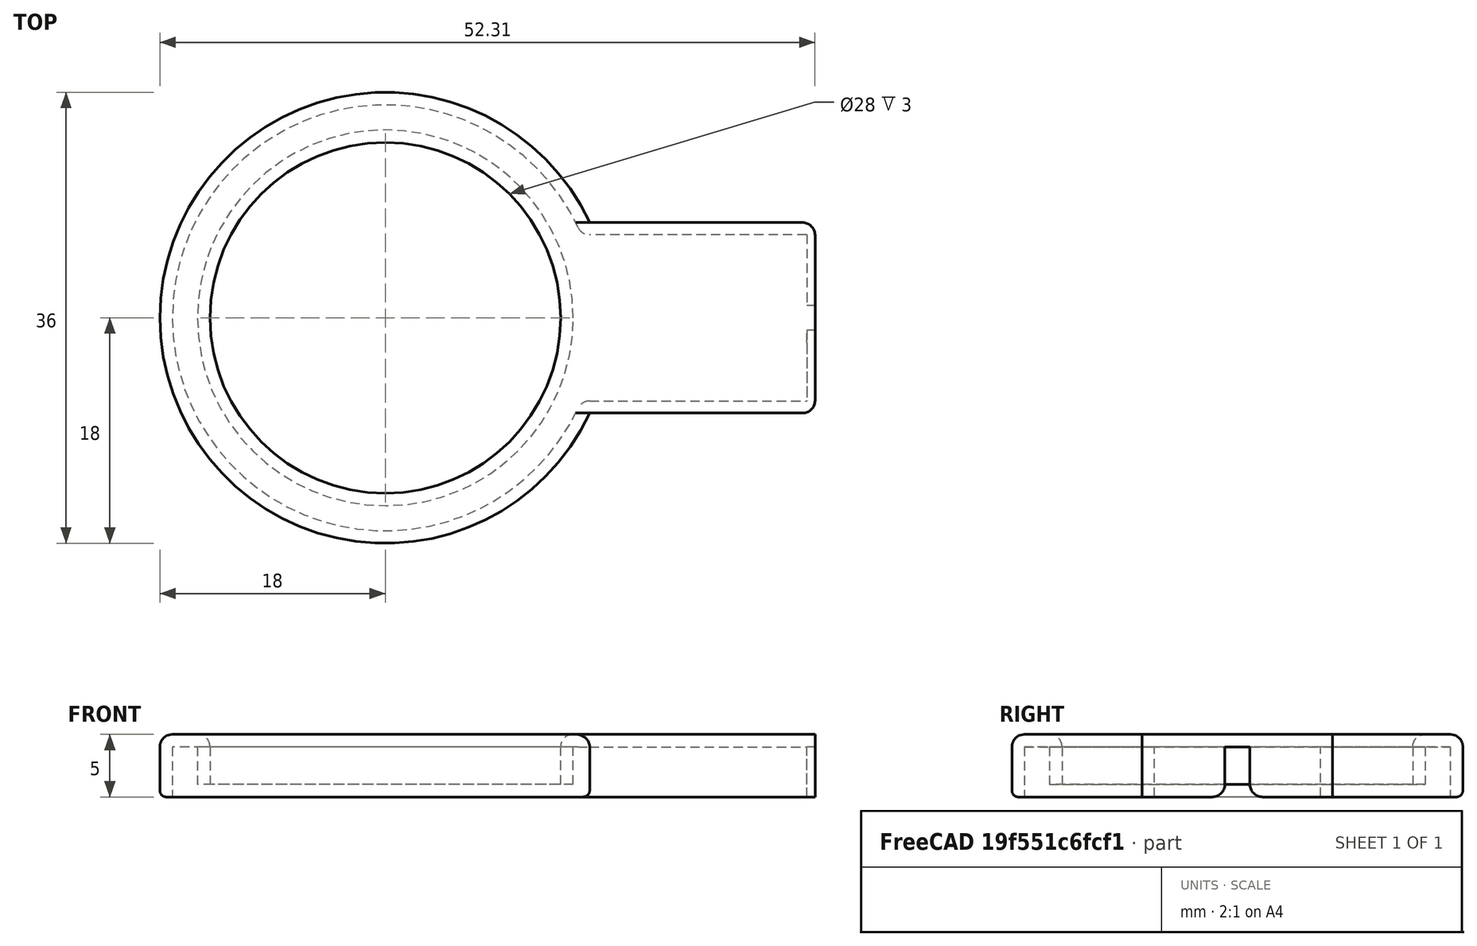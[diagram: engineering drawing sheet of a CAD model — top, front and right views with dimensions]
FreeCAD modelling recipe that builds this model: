
FCSTD DOCUMENT  (FreeCAD 0.19R24291 (Git))
Label: bruker7t_fus_single_coil2_case
License: All rights reserved
LicenseURL: http://en.wikipedia.org/wiki/All_rights_reserved
objects: PartDesign::Fillet×9, TechDraw::DrawViewDimension×7, Sketcher::SketchObject×4, PartDesign::Pad×2, PartDesign::Pocket×2, App::Part×1, PartDesign::Body×1, TechDraw::DrawSVGTemplate×1, TechDraw::DrawViewPart×1, TechDraw::DrawPage×1
note: 31 computed .brp shape members not serialized (recipe doc carries the construction recipe); baked Part::Feature solids carry a one-line shape summary decoded from their .brp

FEATURE [Sketcher::SketchObject] Sketch001
  FullyConstrained = true
  MapMode = 5
  sketch-geometry (5):
    g0: LineSegment StartX=29.3135 StartY=7.60713 StartZ=0 EndX=11.3135 EndY=7.60713 EndZ=0
    g1: ArcOfCircle CenterX=-5 CenterY=-1.8e-15 CenterZ=0 NormalX=0 NormalY=0 NormalZ=1 AngleXU=0 Radius=18 StartAngle=0.436332 EndAngle=5.84685
    g2: LineSegment StartX=11.3135 StartY=-7.60713 StartZ=0 EndX=29.3135 EndY=-7.60713 EndZ=0
    g3: LineSegment StartX=-5 StartY=-1.8e-15 StartZ=0 EndX=11.3135 EndY=7.60713 EndZ=0
    g4: LineSegment StartX=29.3135 StartY=7.60713 StartZ=0 EndX=29.3135 EndY=-7.60713 EndZ=0
  constraints (15):
    c: Horizontal(g0)
    c: Coincident(g1,g2)
    c: Horizontal(g2)
    c: Equal(g0,g2)
    c: PointOnObject(g1,g-1)
    c: Radius(g1) = 18
    c: Coincident(g0,g1)
    c: Coincident(g3,g1)
    c: Coincident(g3,g0)
    c: Angle(g-1,g3) = 0.436332
    c: DistanceX(g1,g-1) = 5
    c: DistanceX(g2,g2) = 18
    c: Coincident(g4,g0)
    c: Coincident(g4,g2)
    c: Symmetric(g0,g2,g-1)
FEATURE [Sketcher::SketchObject] Sketch004
  FullyConstrained = true
  MapMode = 5
  sketch-geometry (10):
    g0: Circle CenterX=-5 CenterY=-2.84e-14 CenterZ=0 NormalX=0 NormalY=0 NormalZ=1 AngleXU=0 Radius=16
    g1: LineSegment StartX=28.6486 StartY=6.64243 StartZ=0 EndX=10.6486 EndY=6.64243 EndZ=0
    g2: ArcOfCircle CenterX=-5 CenterY=-2.84e-14 CenterZ=0 NormalX=0 NormalY=0 NormalZ=1 AngleXU=0 Radius=17 StartAngle=0.401426 EndAngle=5.88176
    g3: LineSegment StartX=10.6486 StartY=-6.64243 StartZ=0 EndX=28.6486 EndY=-6.64243 EndZ=0
    g4: LineSegment StartX=10.6486 StartY=-6.64243 StartZ=0 EndX=-5 EndY=-2.84e-14 EndZ=0
    g5: LineSegment StartX=28.6486 StartY=6.64243 StartZ=0 EndX=28.6486 EndY=1 EndZ=0
    g6: LineSegment StartX=28.6486 StartY=1 StartZ=0 EndX=32.6486 EndY=1 EndZ=0
    g7: LineSegment StartX=32.6486 StartY=1 StartZ=0 EndX=32.6486 EndY=-1 EndZ=0
    g8: LineSegment StartX=32.6486 StartY=-1 StartZ=0 EndX=28.6486 EndY=-1 EndZ=0
    g9: LineSegment StartX=28.6486 StartY=-1 StartZ=0 EndX=28.6486 EndY=-6.64243 EndZ=0
  constraints (27):
    c: Radius(g0) = 16
    c: DistanceX(g0,g-1) = 5
    c: Horizontal(g1)
    c: Coincident(g2,g3)
    c: Horizontal(g3)
    c: Coincident(g2,g1)
    c: Coincident(g2,g0)
    c: Radius(g2) = 17
    c: Symmetric(g2,g1,g-1)
    c: DistanceX(g1,g1) = 18
    c: Coincident(g4,g2)
    c: Coincident(g4,g2)
    c: Angle(g4,g-1) = 0.401426
    c: Equal(g3,g1)
    c: Coincident(g1,g5)
    c: Vertical(g5)
    c: Coincident(g5,g6)
    c: Horizontal(g6)
    c: Coincident(g6,g7)
    c: Coincident(g7,g8)
    c: Horizontal(g8)
    c: Coincident(g8,g9)
    c: Coincident(g9,g3)
    c: Vertical(g9)
    c: Symmetric(g6,g7,g-1)
    c: DistanceY(g7,g7) = 2
    c: DistanceX(g6,g6) = 4
FEATURE [App::Part] Part
  Origin = -> Origin
FEATURE [PartDesign::Pad] Pad
  Direction = (1,1,1)
  Length = 5
  Length2 = 100
  Profile = -> Sketch001
  Refine = true
  Type = 0
FEATURE [PartDesign::Pocket] Pocket
  BaseFeature = -> Pad
  Length = 4
  Length2 = 100
  Profile = -> Sketch004
  Refine = true
  Reversed = true
  Type = 0
FEATURE [Sketcher::SketchObject] Sketch005
  FullyConstrained = true
  MapMode = 5
  Placement = pos=(0,0,1) rot=(0,0,1;0rad)
  sketch-geometry (2):
    g0: Circle CenterX=-5 CenterY=0 CenterZ=0 NormalX=0 NormalY=0 NormalZ=1 AngleXU=0 Radius=16
    g1: Circle CenterX=-5 CenterY=0 CenterZ=0 NormalX=0 NormalY=0 NormalZ=1 AngleXU=0 Radius=15
  constraints (5):
    c: Radius(g0) = 16
    c: PointOnObject(g0,g-1)
    c: DistanceX(g0,g-1) = 5
    c: Coincident(g0,g1)
    c: Radius(g1) = 15
FEATURE [Sketcher::SketchObject] Sketch006
  FullyConstrained = true
  MapMode = 5
  sketch-geometry (2):
    g0: Circle CenterX=-5 CenterY=0 CenterZ=0 NormalX=0 NormalY=0 NormalZ=1 AngleXU=0 Radius=16
    g1: Circle CenterX=-5 CenterY=0 CenterZ=0 NormalX=0 NormalY=0 NormalZ=1 AngleXU=0 Radius=14
  constraints (5):
    c: Radius(g0) = 16
    c: PointOnObject(g0,g-1)
    c: DistanceX(g0,g-1) = 5
    c: Coincident(g0,g1)
    c: Radius(g1) = 14
FEATURE [PartDesign::Pad] Pad001
  BaseFeature = -> Pocket
  Direction = (1,1,1)
  Length = 4
  Length2 = 100
  Profile = -> Sketch005
  Refine = true
  Type = 0
FEATURE [PartDesign::Fillet] Fillet
  Base = -> Pad001 [Edge14]
  BaseFeature = -> Pad001
  Radius = 1
  Refine = true
  SupportTransform = false
FEATURE [PartDesign::Fillet] Fillet001
  Base = -> Fillet [Edge8]
  BaseFeature = -> Fillet
  Radius = 0.5
  Refine = true
  SupportTransform = false
FEATURE [PartDesign::Pocket] Pocket001
  BaseFeature = -> Fillet001
  Length = 5
  Length2 = 100
  Profile = -> Sketch006
  Refine = true
  Reversed = true
  Type = 1
FEATURE [PartDesign::Fillet] Fillet002
  Base = -> Pocket001 [Edge30]
  BaseFeature = -> Pocket001
  Radius = 1
  Refine = true
  SupportTransform = false
FEATURE [PartDesign::Fillet] Fillet003
  Base = -> Fillet002 [Edge32]
  BaseFeature = -> Fillet002
  Radius = 1
  Refine = true
  SupportTransform = false
FEATURE [PartDesign::Fillet] Fillet004
  Base = -> Fillet003 [Edge21]
  BaseFeature = -> Fillet003
  Radius = 1
  Refine = true
  SupportTransform = false
FEATURE [PartDesign::Fillet] Fillet005
  Base = -> Fillet004 [Edge10]
  BaseFeature = -> Fillet004
  Radius = 1
  Refine = true
  SupportTransform = false
FEATURE [PartDesign::Fillet] Fillet006
  Base = -> Fillet005 [Edge3]
  BaseFeature = -> Fillet005
  Radius = 1
  Refine = true
  SupportTransform = false
FEATURE [PartDesign::Fillet] Fillet007
  Base = -> Fillet006 [Edge61]
  BaseFeature = -> Fillet006
  Radius = 1
  Refine = true
  SupportTransform = false
FEATURE [PartDesign::Fillet] Fillet008
  Base = -> Fillet007 [Edge19]
  BaseFeature = -> Fillet007
  Radius = 1
  Refine = true
  SupportTransform = false
FEATURE [PartDesign::Body] Body
  Group = -> [Sketch001,Pad,Sketch004,Pocket,Sketch005,Sketch006,Pad001,Fillet,Fillet001,Pocket001,Fillet002,Fillet003,Fillet004,Fillet005,Fillet006,Fillet007,Fillet008]
  Origin = -> Origin001
  Tip = -> Fillet008
FEATURE [TechDraw::DrawSVGTemplate] Template
  Height = 297
  Orientation = 1
  Width = 420
FEATURE [TechDraw::DrawViewPart] View
  CoarseView = false
  Direction = (0,0,1)
  Focus = 100
  HardHidden = false
  IsoCount = 0
  IsoHidden = false
  IsoVisible = false
  LockPosition = false
  Perspective = false
  Rotation = 0
  Scale = 2
  ScaleType = 0
  SeamHidden = false
  SeamVisible = true
  SmoothHidden = false
  SmoothVisible = true
  Source = -> [Body]
  X = 97.7577
  XDirection = (1,0,0)
  Y = 169.358
FEATURE [TechDraw::DrawViewDimension] Dimension
  Arbitrary = false
  ArbitraryTolerances = false
  EqualTolerance = true
  FormatSpec = %.2f
  FormatSpecOverTolerance = %+.2f
  FormatSpecUnderTolerance = %+.2f
  Inverted = false
  LockPosition = false
  MeasureType = 1
  OverTolerance = 0
  References2D = -> [View]
  Rotation = 0
  ScaleType = 0
  TheoreticalExact = false
  Type = 2
  UnderTolerance = 0
  X = 43.3787
  Y = -1.0347
FEATURE [TechDraw::DrawViewDimension] Dimension001
  Arbitrary = false
  ArbitraryTolerances = false
  EqualTolerance = true
  FormatSpec = R%.2f
  FormatSpecOverTolerance = %+.2f
  FormatSpecUnderTolerance = %+.2f
  Inverted = false
  LockPosition = false
  MeasureType = 1
  OverTolerance = 0
  References2D = -> [View]
  Rotation = 0
  ScaleType = 0
  TheoreticalExact = false
  Type = 4
  UnderTolerance = 0
  X = 0
  Y = 0
FEATURE [TechDraw::DrawViewDimension] Dimension002
  Arbitrary = false
  ArbitraryTolerances = false
  EqualTolerance = true
  FormatSpec = R%.2f
  FormatSpecOverTolerance = %+.2f
  FormatSpecUnderTolerance = %+.2f
  Inverted = false
  LockPosition = false
  MeasureType = 1
  OverTolerance = 0
  References2D = -> [View]
  Rotation = 0
  ScaleType = 0
  TheoreticalExact = false
  Type = 4
  UnderTolerance = 0
  X = -28.1668
  Y = 0.6898
FEATURE [TechDraw::DrawViewDimension] Dimension003
  Arbitrary = false
  ArbitraryTolerances = false
  EqualTolerance = true
  FormatSpec = %.2f
  FormatSpecOverTolerance = %+.2f
  FormatSpecUnderTolerance = %+.2f
  Inverted = false
  LockPosition = false
  MeasureType = 1
  OverTolerance = 0
  References2D = -> [View]
  Rotation = 0
  ScaleType = 0
  TheoreticalExact = false
  Type = 1
  UnderTolerance = 0
  X = 35.2356
  Y = 26.8606
FEATURE [TechDraw::DrawViewDimension] Dimension004
  Arbitrary = false
  ArbitraryTolerances = false
  EqualTolerance = true
  FormatSpec = R%.2f
  FormatSpecOverTolerance = %+.2f
  FormatSpecUnderTolerance = %+.2f
  Inverted = false
  LockPosition = false
  MeasureType = 1
  OverTolerance = 0
  References2D = -> [View]
  Rotation = 0
  ScaleType = 0
  TheoreticalExact = false
  Type = 4
  UnderTolerance = 0
  X = -29.1116
  Y = -15.2276
FEATURE [TechDraw::DrawViewDimension] Dimension005
  Arbitrary = false
  ArbitraryTolerances = false
  EqualTolerance = true
  FormatSpec = R%.2f
  FormatSpecOverTolerance = %+.2f
  FormatSpecUnderTolerance = %+.2f
  Inverted = false
  LockPosition = false
  MeasureType = 1
  OverTolerance = 0
  References2D = -> [View]
  Rotation = 0
  ScaleType = 0
  TheoreticalExact = false
  Type = 4
  UnderTolerance = 0
  X = -7.61381
  Y = -9.62923
FEATURE [TechDraw::DrawViewDimension] Dimension006
  Arbitrary = false
  ArbitraryTolerances = false
  EqualTolerance = true
  FormatSpec = R%.2f
  FormatSpecOverTolerance = %+.2f
  FormatSpecUnderTolerance = %+.2f
  Inverted = false
  LockPosition = false
  MeasureType = 1
  OverTolerance = 0
  References2D = -> [View]
  Rotation = 0
  ScaleType = 0
  TheoreticalExact = false
  Type = 4
  UnderTolerance = 0
  X = 0
  Y = 0
FEATURE [TechDraw::DrawPage] Page
  KeepUpdated = true
  NextBalloonIndex = 1
  ProjectionType = 0
  Template = -> Template
  Views = -> [View,Dimension,Dimension001,Dimension002,Dimension003,Dimension004,Dimension005,Dimension006]
